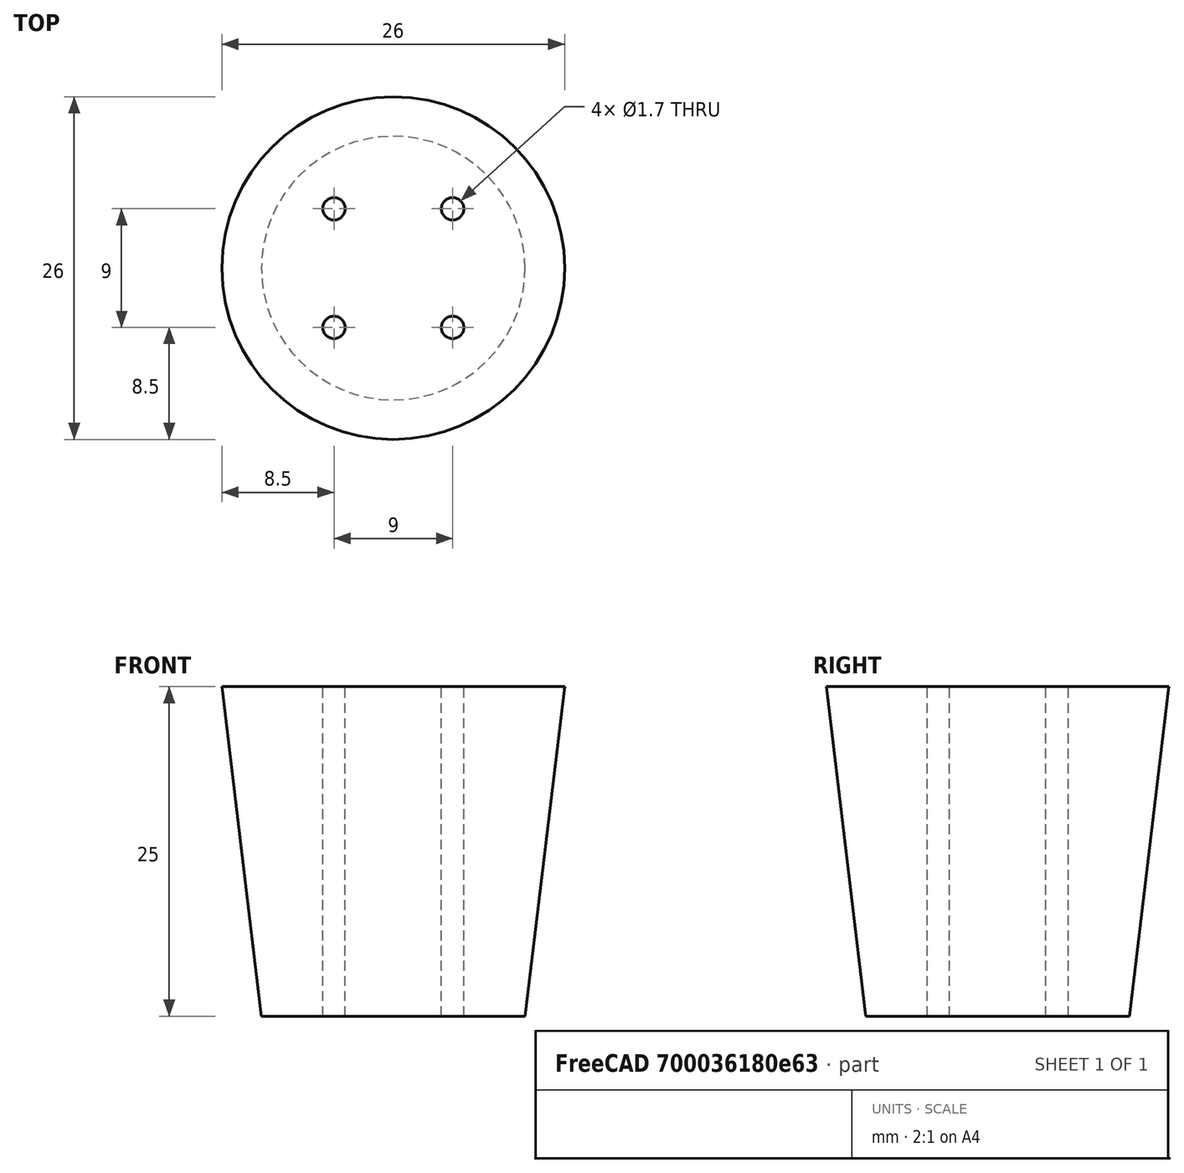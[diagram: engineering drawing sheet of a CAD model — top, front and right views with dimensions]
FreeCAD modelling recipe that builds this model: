
FCSTD DOCUMENT  (FreeCAD 0.18R15938 (Git))
Label: plug
License: All rights reserved
LicenseURL: http://en.wikipedia.org/wiki/All_rights_reserved
objects: Drawing::FeatureViewPython×13, TechDraw::DrawViewDimension×9, TechDraw::DrawProjGroupItem×6, TechDraw::DrawSVGTemplate×3, Drawing::FeatureViewPart×3, TechDraw::DrawPage×3, TechDraw::DrawProjGroup×2, PartDesign::AdditiveCone×1, PartDesign::SubtractiveCylinder×1, PartDesign::PolarPattern×1, PartDesign::Body×1, Drawing::FeaturePage×1, TechDraw::DrawGeomHatch×1, TechDraw::DrawViewSection×1, TechDraw::DrawViewAnnotation×1
note: 6 computed .brp shape members not serialized (recipe doc carries the construction recipe); baked Part::Feature solids carry a one-line shape summary decoded from their .brp

FEATURE [PartDesign::AdditiveCone] Cone
  Angle = 360
  AttacherType = Attacher::AttachEngine3D
  Height = 25
  Radius1 = 10
  Radius2 = 13
FEATURE [PartDesign::SubtractiveCylinder] Cylinder001  label="hole"
  Angle = 360
  AttacherType = Attacher::AttachEngine3D
  AttachmentOffset = pos=(4.5,4.5,0) rot=(0,0,1;0rad)
  BaseFeature = -> Cone
  Height = 50
  MapMode = 5
  Placement = pos=(4.5,4.5,0) rot=(0,0,1;0rad)
  Radius = 0.85
  Support = -> [XY_Plane]
FEATURE [PartDesign::PolarPattern] PolarPattern
  Angle = 360
  Axis = -> Z_Axis
  BaseFeature = -> Cylinder001
  Occurrences = 4
  Originals = -> [Cylinder001]
  Placement = pos=(4.5,4.5,0) rot=(0,0,1;0rad)
FEATURE [PartDesign::Body] Body
  Group = -> [Cone,Cylinder001,PolarPattern]
  Origin = -> Origin
  Tip = -> PolarPattern
FEATURE [TechDraw::DrawSVGTemplate] Template
  EditableTexts = Designed_by_Name=Christian <owner>; Drawing_number=2; FC-Date=21.2.2019; FC-SC=2:1; FC-SH=1; FC-Title=Title; Subtitle=silicone plug; Weight=Weight
  Height = 210
  Orientation = 1
  Width = 297
FEATURE [TechDraw::DrawProjGroupItem] ProjItem
  CoarseView = false
  Direction = (0,-1,0)
  Focus = 100
  HardHidden = true
  IsoCount = 0
  IsoHidden = true
  IsoVisible = false
  LockPosition = true
  Perspective = false
  Rotation = 0
  RotationVector = (1,0,0)
  Scale = 2
  ScaleType = 2
  SeamHidden = false
  SeamVisible = true
  SmoothHidden = true
  SmoothVisible = false
  Source = -> [PolarPattern]
  Type = 0
  X = 0
  Y = 0
FEATURE [TechDraw::DrawProjGroupItem] ProjItem003
  CoarseView = false
  Direction = (1,-1,-1)
  Focus = 100
  HardHidden = false
  IsoCount = 0
  IsoHidden = false
  IsoVisible = false
  LockPosition = true
  Perspective = false
  Rotation = 0
  RotationVector = (1,1,0)
  Scale = 2
  ScaleType = 2
  SeamHidden = false
  SeamVisible = false
  SmoothHidden = false
  SmoothVisible = false
  Source = -> [PolarPattern]
  Type = 9
  X = 124.084
  Y = -2.07724
FEATURE [TechDraw::DrawProjGroupItem] ProjItem004
  CoarseView = false
  Direction = (0,0,1)
  Focus = 100
  HardHidden = false
  IsoCount = 1
  IsoHidden = false
  IsoVisible = false
  LockPosition = false
  Perspective = false
  Rotation = 0
  RotationVector = (1,0,0)
  Scale = 2
  ScaleType = 2
  SeamHidden = false
  SeamVisible = false
  SmoothHidden = false
  SmoothVisible = false
  Source = -> [PolarPattern]
  Type = 4
  X = 0
  Y = -82.3829
FEATURE [TechDraw::DrawProjGroup] ProjGroup
  Anchor = -> ProjItem
  AutoDistribute = true
  LockPosition = false
  ProjectionType = 0
  Rotation = 0
  Scale = 2
  ScaleType = 2
  Source = -> [PolarPattern]
  Views = -> [ProjItem,ProjItem003,ProjItem004]
  X = 78.42
  Y = 143.503
  spacingX = 15
  spacingY = 15
FEATURE [TechDraw::DrawViewDimension] Dimension001
  Arbitrary = false
  FormatSpec = %.2f
  LockPosition = false
  MeasureType = 1
  OverTolerance = 0
  References2D = -> [ProjItem]
  Rotation = 0
  ScaleType = 0
  Type = 1
  UnderTolerance = 0
  X = 0.238546
  Y = -38.9683
FEATURE [TechDraw::DrawViewDimension] Dimension002
  Arbitrary = false
  FormatSpec = %.2f
  LockPosition = false
  MeasureType = 1
  OverTolerance = 0
  References2D = -> [ProjItem]
  Rotation = 0
  ScaleType = 0
  Type = 1
  UnderTolerance = 0
  X = 1.55225
  Y = 47.0944
FEATURE [TechDraw::DrawViewDimension] Dimension004
  Arbitrary = false
  FormatSpec = %.2f
  LockPosition = false
  MeasureType = 1
  OverTolerance = 0
  References2D = -> [ProjItem]
  Rotation = 0
  ScaleType = 0
  Type = 2
  UnderTolerance = 0
  X = -44.7315
  Y = -2.79405
FEATURE [TechDraw::DrawViewDimension] Dimension005
  Arbitrary = false
  FormatSpec = %.2f
  LockPosition = false
  MeasureType = 1
  OverTolerance = 0
  References2D = -> [ProjItem]
  Rotation = 0
  ScaleType = 0
  Type = 1
  UnderTolerance = 0
  X = -40.1485
  Y = 33.3646
FEATURE [TechDraw::DrawViewDimension] Dimension006
  Arbitrary = false
  FormatSpec = %.2f
  LockPosition = false
  MeasureType = 1
  OverTolerance = 0
  References2D = -> [ProjItem]
  Rotation = 0
  ScaleType = 0
  Type = 1
  UnderTolerance = 0
  X = 44.3913
  Y = 33.3822
FEATURE [Drawing::FeatureViewPart] Ortho  label="Ortho_0_0"
  Direction = (1,0,0)
  HiddenWidth = 0.15
  LineWidth = 0.35
  Rotation = -90
  Scale = 4
  ShowHiddenLines = true
  ShowSmoothLines = false
  Source = -> PolarPattern
  Tolerance = 0.05
  ViewResult = <blob: 8468 chars omitted>
  Visible = true
  X = 120
  Y = 264.67
FEATURE [Drawing::FeatureViewPart] Ortho002  label="Ortho_0_1"
  Direction = (0,0,1)
  HiddenWidth = 0.15
  LineWidth = 0.35
  Rotation = 90
  Scale = 4
  ShowHiddenLines = true
  ShowSmoothLines = false
  Source = -> PolarPattern
  Tolerance = 0.05
  ViewResult = <g id="Ortho_0_1"\n   transform="rotate(90,120,80.33) translate(120,80.33) scale(4,4)"\n  >\n<g   fill="none"\n   stroke="rgb(0, 0, 0)"\n   stroke-dasharray="0.2,0.1)"\n   stroke-linecap="butt"\n   stroke-linejoin="miter"\n   stroke-width="0.037500"\n   transform="scale(1,-1)"\n  >\n<circle cx ="0" cy ="0" r ="10" /><circle cx ="-4.5" cy ="-4.5" r ="0.85" /><circle cx ="4.5" cy ="-4.5" r ="0.85" /><circle cx ="4.5" cy ="4.5" r ="0.85" /><circle cx ="-4.5" cy ="4.5" r ="0.85" /></g>\n<g   fill="none"\n   stroke="rgb(0, 0, 0)"\n   stroke-linecap="butt"\n   stroke-linejoin="miter"\n   stroke-width="0.087500"\n   transform="scale(1,-1)"\n  >\n<circle cx ="0" cy ="0" r ="13" /><circle cx ="-4.5" cy ="-4.5" r ="0.85" /><circle cx ="4.5" cy ="-4.5" r ="0.85" /><circle cx ="-4.5" cy ="4.5" r ="0.85" /><circle cx ="4.5" cy ="4.5" r ="0.85" /></g>\n</g>
  Visible = true
  X = 120
  Y = 80.33
FEATURE [Drawing::FeatureViewPart] Ortho003  label="Ortho_1_1"
  Direction = (0.57735,0.57735,0.57735)
  HiddenWidth = 0.15
  LineWidth = 0.35
  Rotation = 120
  Scale = 4
  ShowHiddenLines = true
  ShowSmoothLines = false
  Source = -> PolarPattern
  Tolerance = 0.05
  ViewResult = <blob: 3528 chars omitted>
  Visible = true
  X = 294
  Y = 139.16
FEATURE [Drawing::FeatureViewPython] dim002  # drawing view (typed FeaturePython)
  Rotation = 0
  ViewResult = <g> \n  <line x1="118.000000" y1="132.330000" x2="37.053954" y2="132.330000" style="stroke:rgb(0,0,255);stroke-width:0.50" />\n<line x1="118.000000" y1="28.330000" x2="37.053954" y2="28.330000" style="stroke:rgb(0,0,255);stroke-width:0.50" />\n<line x1="38.053954" y1="132.330000" x2="38.053954" y2="28.330000" style="stroke:rgb(0,0,255);stroke-width:0.50" /> \n  <polygon points="38.053954,28.330000 37.053954,31.330000 38.053954,32.330000 39.053954,31.330000" style="fill:rgb(0,0,255);stroke:rgb(0,0,255);stroke-width:0" /><polygon points="38.053954,132.330000 39.053954,129.330000 38.053954,128.330000 37.053954,129.330000" style="fill:rgb(0,0,255);stroke:rgb(0,0,255);stroke-width:0" /> \n  <text x="36.053954" y="80.330000" font-family="inherit" font-size="3.6" fill="rgb(0,0,255)" text-anchor="middle" transform="rotate(-90.000000 36.053954,80.330000)" >26</text> </g>
  Visible = true
  X = 0
  Y = 0
  arrowL1 = 3
  arrowL2 = 1
  arrowW = 2
  arrow_scheme = 0
  autoPlaceOffset = 2
  autoPlaceText = true
  click1_x = 38.054
  click1_y = 40.1287
  click2_x = 38.054
  click2_y = 40.1287
  comma_decimal_place = false
  dimension_line_overshoot = 1
  gap_datum_points = 2
  halfDimension_linear = false
  lineColor = rgb(0,0,255)
  strokeWidth = 0.5
  textFormat_linear = %(value)3.3f
  textRenderer_color = rgb(0,0,255)
  textRenderer_family = inherit
  textRenderer_size = 3.6
  unit_custom_scale = 1
  unit_scheme = 0
FEATURE [Drawing::FeatureViewPython] dim004  # drawing view (typed FeaturePython)
  Rotation = 0
  ViewResult = <g> \n  <line x1="66.326800" y1="164.670000" x2="51.366021" y2="164.670000" style="stroke:rgb(0,0,255);stroke-width:0.50" />\n<line x1="78.251520" y1="264.670000" x2="51.366021" y2="264.670000" style="stroke:rgb(0,0,255);stroke-width:0.50" />\n<line x1="52.366021" y1="164.670000" x2="52.366021" y2="264.670000" style="stroke:rgb(0,0,255);stroke-width:0.50" /> \n  <polygon points="52.366021,264.670000 53.366021,261.670000 52.366021,260.670000 51.366021,261.670000" style="fill:rgb(0,0,255);stroke:rgb(0,0,255);stroke-width:0" /><polygon points="52.366021,164.670000 51.366021,167.670000 52.366021,168.670000 53.366021,167.670000" style="fill:rgb(0,0,255);stroke:rgb(0,0,255);stroke-width:0" /> \n  <text x="50.366021" y="214.670000" font-family="inherit" font-size="3.6" fill="rgb(0,0,255)" text-anchor="middle" transform="rotate(-90.000000 50.366021,214.670000)" >25</text> </g>
  Visible = true
  X = 0
  Y = 0
  arrowL1 = 3
  arrowL2 = 1
  arrowW = 2
  arrow_scheme = 0
  autoPlaceOffset = 2
  autoPlaceText = true
  click1_x = 52.366
  click1_y = 213.983
  click2_x = 52.366
  click2_y = 213.983
  comma_decimal_place = false
  dimension_line_overshoot = 1
  gap_datum_points = 2
  halfDimension_linear = false
  lineColor = rgb(0,0,255)
  strokeWidth = 0.5
  textFormat_linear = %(value)3.3f
  textRenderer_color = rgb(0,0,255)
  textRenderer_family = inherit
  textRenderer_size = 3.6
  unit_custom_scale = 1
  unit_scheme = 0
FEATURE [TechDraw::DrawSVGTemplate] Template001
  EditableTexts = Designed_by_Name=Designed by Name; Drawing_number=Drawing number; FC-Date=Date; FC-SC=Scale; FC-SH=Sheet; FC-Title=Title; Subtitle=Subtitle; Weight=Weight
  Height = 210
  Orientation = 1
  Width = 297
FEATURE [TechDraw::DrawProjGroupItem] ProjItem005  label="Front"
  CoarseView = false
  Direction = (0,-1,0)
  Focus = 100
  HardHidden = false
  IsoCount = 0
  IsoHidden = false
  IsoVisible = false
  LockPosition = true
  Perspective = false
  Rotation = 0
  RotationVector = (1,0,0)
  Scale = 2
  ScaleType = 2
  SeamHidden = false
  SeamVisible = false
  SmoothHidden = false
  SmoothVisible = false
  Source = -> [PolarPattern]
  Type = 0
  X = 0
  Y = 0
FEATURE [TechDraw::DrawProjGroupItem] ProjItem007  label="Bottom"
  CoarseView = false
  Direction = (0,0,-1)
  Focus = 100
  HardHidden = false
  IsoCount = 0
  IsoHidden = false
  IsoVisible = false
  LockPosition = false
  Perspective = false
  Rotation = 0
  RotationVector = (1,0,0)
  Scale = 2
  ScaleType = 2
  SeamHidden = false
  SeamVisible = false
  SmoothHidden = false
  SmoothVisible = false
  Source = -> [PolarPattern]
  Type = 5
  X = 0
  Y = 82.3829
FEATURE [TechDraw::DrawProjGroupItem] ProjItem008  label="FrontBottomLeft"
  CoarseView = false
  Direction = (-1,-1,-1)
  Focus = 100
  HardHidden = false
  IsoCount = 0
  IsoHidden = false
  IsoVisible = false
  LockPosition = false
  Perspective = false
  Rotation = 0
  RotationVector = (1,-1,0)
  Scale = 2
  ScaleType = 2
  SeamHidden = false
  SeamVisible = false
  SmoothHidden = false
  SmoothVisible = false
  Source = -> [PolarPattern]
  Type = 8
  X = 82.3829
  Y = 82.3829
FEATURE [TechDraw::DrawProjGroup] ProjGroup001
  Anchor = -> ProjItem005
  AutoDistribute = true
  LockPosition = false
  ProjectionType = 0
  Rotation = 0
  Scale = 2
  ScaleType = 0
  Source = -> [PolarPattern]
  Views = -> [ProjItem005,ProjItem007,ProjItem008]
  X = 62.8611
  Y = 69.42
  spacingX = 15
  spacingY = 15
FEATURE [TechDraw::DrawViewDimension] Dimension
  Arbitrary = false
  FormatSpec = %.2f
  LockPosition = false
  MeasureType = 1
  OverTolerance = 0
  References2D = -> [ProjItem005]
  Rotation = 0
  ScaleType = 0
  Type = 1
  UnderTolerance = 0
  X = 0.359317
  Y = -30.542
FEATURE [Drawing::FeatureViewPython] centerLines001  # drawing view (typed FeaturePython)
  Rotation = 0
  ViewResult = <g transform="scale(4.000000,4.000000)" stroke="rgb(0,0,255)"  stroke-width="0.080000" > <path d="M 35.350000,24.582500 L 35.350000,25.332500 M 35.350000,25.832500 L 35.350000,27.332500 M 35.350000,27.832500 L 35.350000,28.582500 M 35.350000,29.082500 L 35.350000,30.582500 M 35.350000,31.082500 L 35.350000,31.832500 M 35.350000,32.332500 L 35.350000,33.832500 M 35.350000,34.332500 L 35.350000,35.082500 M 35.350000,35.582500 L 35.350000,36.548504 "/>\n<path d="M 35.350000,24.582500 L 35.350000,25.332500 M 35.350000,25.832500 L 35.350000,27.332500 M 35.350000,27.832500 L 35.350000,28.582500 M 35.350000,29.082500 L 35.350000,30.582500 M 35.350000,31.082500 L 35.350000,31.832500 M 35.350000,32.332500 L 35.350000,33.832500 M 35.350000,34.332500 L 35.350000,35.082500 "/> </g> 
  Visible = true
  X = 0
  Y = 0
  centerLine_color = rgb(0,0,255)
  centerLine_len_dash = 6
  centerLine_len_dot = 3
  centerLine_len_gap = 2
  centerLine_width = 0.32
  click1_x = 136.029
  click1_y = 146.194
  click2_x = 153.742
  click2_y = 140.618
FEATURE [Drawing::FeatureViewPython] centerLines002  # drawing view (typed FeaturePython)
  Rotation = 0
  ViewResult = <g transform="scale(4.000000,4.000000)" stroke="rgb(0,0,255)"  stroke-width="0.080000" > <path d="M 33.650000,24.582500 L 33.650000,25.332500 M 33.650000,25.832500 L 33.650000,27.332500 M 33.650000,27.832500 L 33.650000,28.582500 M 33.650000,29.082500 L 33.650000,30.582500 M 33.650000,31.082500 L 33.650000,31.832500 M 33.650000,32.332500 L 33.650000,33.832500 M 33.650000,34.332500 L 33.650000,35.082500 M 33.650000,35.582500 L 33.650000,36.630507 "/>\n<path d="M 33.650000,24.582500 L 33.650000,25.332500 M 33.650000,25.832500 L 33.650000,27.332500 M 33.650000,27.832500 L 33.650000,28.266215 "/> </g> 
  Visible = true
  X = 0
  Y = 0
  centerLine_color = rgb(0,0,255)
  centerLine_len_dash = 6
  centerLine_len_dot = 3
  centerLine_len_gap = 2
  centerLine_width = 0.32
  click1_x = 139.309
  click1_y = 146.522
  click2_x = 165.55
  click2_y = 113.065
FEATURE [Drawing::FeatureViewPython] centerLines003  # drawing view (typed FeaturePython)
  Rotation = 0
  ViewResult = <g transform="scale(4.000000,4.000000)" stroke="rgb(0,0,255)"  stroke-width="0.080000" > <path d="M 26.350000,24.582500 L 26.350000,25.332500 M 26.350000,25.832500 L 26.350000,27.332500 M 26.350000,27.832500 L 26.350000,28.582500 M 26.350000,29.082500 L 26.350000,30.582500 M 26.350000,31.082500 L 26.350000,31.832500 M 26.350000,32.332500 L 26.350000,33.832500 M 26.350000,34.332500 L 26.350000,35.082500 M 26.350000,35.582500 L 26.350000,36.630507 "/>\n<path d="M 26.350000,24.582500 L 26.350000,25.332500 M 26.350000,25.832500 L 26.350000,27.332500 M 26.350000,27.832500 L 26.350000,28.582500 M 26.350000,29.082500 L 26.350000,30.582500 M 26.350000,31.082500 L 26.350000,31.832500 M 26.350000,32.332500 L 26.350000,33.832500 M 26.350000,34.332500 L 26.350000,35.082500 M 26.350000,35.582500 L 26.350000,36.712510 "/> </g> 
  Visible = true
  X = 0
  Y = 0
  centerLine_color = rgb(0,0,255)
  centerLine_len_dash = 6
  centerLine_len_dot = 3
  centerLine_len_gap = 2
  centerLine_width = 0.32
  click1_x = 109.132
  click1_y = 146.522
  click2_x = 108.804
  click2_y = 146.85
FEATURE [Drawing::FeatureViewPython] centerLines004  # drawing view (typed FeaturePython)
  Rotation = 0
  ViewResult = <g transform="scale(4.000000,4.000000)" stroke="rgb(0,0,255)"  stroke-width="0.080000" > <path d="M 24.650000,24.582500 L 24.650000,25.332500 M 24.650000,25.832500 L 24.650000,27.332500 M 24.650000,27.832500 L 24.650000,28.582500 M 24.650000,29.082500 L 24.650000,30.582500 M 24.650000,31.082500 L 24.650000,31.832500 M 24.650000,32.332500 L 24.650000,33.832500 M 24.650000,34.332500 L 24.650000,35.082500 M 24.650000,35.582500 L 24.650000,36.548504 "/>\n<path d="M 24.650000,24.582500 L 24.650000,25.332500 M 24.650000,25.832500 L 24.650000,27.332500 M 24.650000,27.832500 L 24.650000,28.582500 M 24.650000,29.082500 L 24.650000,30.582500 M 24.650000,31.082500 L 24.650000,31.832500 M 24.650000,32.332500 L 24.650000,33.104384 "/> </g> 
  Visible = true
  X = 0
  Y = 0
  centerLine_color = rgb(0,0,255)
  centerLine_len_dash = 6
  centerLine_len_dot = 3
  centerLine_len_gap = 2
  centerLine_width = 0.32
  click1_x = 99.9477
  click1_y = 146.194
  click2_x = 92.4034
  click2_y = 132.418
FEATURE [Drawing::FeatureViewPython] dim005  # drawing view (typed FeaturePython)
  Rotation = 0
  ViewResult = <g> \n  <line x1="160.000000" y1="266.670000" x2="160.000000" y2="283.759200" style="stroke:rgb(0,0,255);stroke-width:0.50" />\n<line x1="80.000000" y1="266.670000" x2="80.000000" y2="283.759200" style="stroke:rgb(0,0,255);stroke-width:0.50" />\n<line x1="160.000000" y1="282.759200" x2="80.000000" y2="282.759200" style="stroke:rgb(0,0,255);stroke-width:0.50" /> \n  <polygon points="80.000000,282.759200 83.000000,283.759200 84.000000,282.759200 83.000000,281.759200" style="fill:rgb(0,0,255);stroke:rgb(0,0,255);stroke-width:0" /><polygon points="160.000000,282.759200 157.000000,281.759200 156.000000,282.759200 157.000000,283.759200" style="fill:rgb(0,0,255);stroke:rgb(0,0,255);stroke-width:0" /> \n  <text x="120.000000" y="280.759200" font-family="inherit" font-size="3.6" fill="rgb(0,0,255)" text-anchor="middle" transform="rotate(-0.000000 120.000000,280.759200)" >20</text> </g>
  Visible = true
  X = 0
  Y = 0
  arrowL1 = 3
  arrowL2 = 1
  arrowW = 2
  arrow_scheme = 0
  autoPlaceOffset = 2
  autoPlaceText = true
  click1_x = 75.5331
  click1_y = 282.759
  click2_x = 75.5331
  click2_y = 282.759
  comma_decimal_place = false
  dimension_line_overshoot = 1
  gap_datum_points = 2
  halfDimension_linear = false
  lineColor = rgb(0,0,255)
  strokeWidth = 0.5
  textFormat_linear = %(value)3.3f
  textRenderer_color = rgb(0,0,255)
  textRenderer_family = inherit
  textRenderer_size = 3.6
  unit_custom_scale = 1.3
  unit_scheme = 0
FEATURE [Drawing::FeatureViewPython] dim001  # drawing view (typed FeaturePython)
  Rotation = 0
  ViewResult = <g> \n  <line x1="68.000000" y1="162.670000" x2="68.000000" y2="156.696284" style="stroke:rgb(0,0,255);stroke-width:0.50" />\n<line x1="172.000000" y1="162.670000" x2="172.000000" y2="156.696284" style="stroke:rgb(0,0,255);stroke-width:0.50" />\n<line x1="68.000000" y1="157.696284" x2="172.000000" y2="157.696284" style="stroke:rgb(0,0,255);stroke-width:0.50" /> \n  <polygon points="172.000000,157.696284 169.000000,156.696284 168.000000,157.696284 169.000000,158.696284" style="fill:rgb(0,0,255);stroke:rgb(0,0,255);stroke-width:0" /><polygon points="68.000000,157.696284 71.000000,158.696284 72.000000,157.696284 71.000000,156.696284" style="fill:rgb(0,0,255);stroke:rgb(0,0,255);stroke-width:0" /> \n  <text x="120.000000" y="155.696284" font-family="inherit" font-size="3.6" fill="rgb(0,0,255)" text-anchor="middle" transform="rotate(0.000000 120.000000,155.696284)" >26</text> </g>
  Visible = true
  X = 0
  Y = 0
  arrowL1 = 3
  arrowL2 = 1
  arrowW = 2
  arrow_scheme = 0
  autoPlaceOffset = 2
  autoPlaceText = true
  click1_x = 163.18
  click1_y = 157.696
  click2_x = 163.18
  click2_y = 157.696
  comma_decimal_place = false
  dimension_line_overshoot = 1
  gap_datum_points = 2
  halfDimension_linear = false
  lineColor = rgb(0,0,255)
  strokeWidth = 0.5
  textFormat_linear = %(value)3.3f
  textRenderer_color = rgb(0,0,255)
  textRenderer_family = inherit
  textRenderer_size = 3.6
  unit_custom_scale = 1
  unit_scheme = 0
FEATURE [Drawing::FeatureViewPython] dia001  # drawing view (typed FeaturePython)
  Rotation = 0
  ViewResult = <g>  <circle cx ="138.000000" cy ="98.330000" r="0.250000" stroke="none" fill="rgb(0,0,255)" /> \n<line x1="164.648471" y1="38.150256" x2="136.623362" y2="101.438837" style="stroke:rgb(0,0,255);stroke-width:0.50" />\n<polygon points="139.376638,95.221163 141.505683,92.882965 140.996213,91.563708 139.676956,92.073178" style="fill:rgb(0,0,255);stroke:rgb(0,0,255);stroke-width:0" />\n<polygon points="136.623362,101.438837 134.494317,103.777035 135.003787,105.096292 136.323044,104.586822" style="fill:rgb(0,0,255);stroke:rgb(0,0,255);stroke-width:0" />\n<line x1="164.648471" y1="38.150256" x2="201.192400" y2="38.150256" style="stroke:rgb(0,0,255);stroke-width:0.50" />\n<text x="182.920436" y="36.150256" font-family="inherit" font-size="3.6" fill="rgb(0,0,255)" text-anchor="middle" transform="rotate(0.000000 182.920436,36.150256)" >Ø1.7</text> </g>
  Visible = false
  X = 0
  Y = 0
  arrowL1 = 3
  arrowL2 = 1
  arrowW = 2
  arrow_scheme = 0
  autoPlaceOffset = 2
  autoPlaceText = true
  centerPointDia = 0.5
  click1_x = 164.648
  click1_y = 38.1503
  click2_x = 201.192
  click2_y = 39.7566
  click3_x = 201.192
  click3_y = 39.7566
  comma_decimal_place = false
  lineColor = rgb(0,0,255)
  strokeWidth = 0.5
  textFormat_circular = Ø%(value)3.3f
  textRenderer_color = rgb(0,0,255)
  textRenderer_family = inherit
  textRenderer_size = 3.6
  unit_custom_scale = 1
  unit_scheme = 0
FEATURE [Drawing::FeatureViewPython] dim003  # drawing view (typed FeaturePython)
  Rotation = 0
  ViewResult = <g> \n  <line x1="134.600000" y1="144.522028" x2="134.600000" y2="137.744965" style="stroke:rgb(0,0,255);stroke-width:0.50" />\n<line x1="141.400000" y1="144.194016" x2="141.400000" y2="137.744965" style="stroke:rgb(0,0,255);stroke-width:0.50" />\n<line x1="134.600000" y1="138.744965" x2="141.400000" y2="138.744965" style="stroke:rgb(0,0,255);stroke-width:0.50" /> \n  <polygon points="141.400000,138.744965 144.400000,139.744965 145.400000,138.744965 144.400000,137.744965" style="fill:rgb(0,0,255);stroke:rgb(0,0,255);stroke-width:0" /><polygon points="134.600000,138.744965 131.600000,137.744965 130.600000,138.744965 131.600000,139.744965" style="fill:rgb(0,0,255);stroke:rgb(0,0,255);stroke-width:0" /> \n  <text x="138.000000" y="136.744965" font-family="inherit" font-size="3.6" fill="rgb(0,0,255)" text-anchor="middle" transform="rotate(0.000000 138.000000,136.744965)" >1.7</text> </g>
  Visible = true
  X = 0
  Y = 0
  arrowL1 = 3
  arrowL2 = 1
  arrowW = 2
  arrow_scheme = 0
  autoPlaceOffset = 2
  autoPlaceText = true
  click1_x = 134.6
  click1_y = 138.745
  click2_x = 134.6
  click2_y = 138.745
  comma_decimal_place = false
  dimension_line_overshoot = 1
  gap_datum_points = 2
  halfDimension_linear = false
  lineColor = rgb(0,0,255)
  strokeWidth = 0.5
  textFormat_linear = %(value)3.3f
  textRenderer_color = rgb(0,0,255)
  textRenderer_family = inherit
  textRenderer_size = 3.6
  unit_custom_scale = 1
  unit_scheme = 0
FEATURE [Drawing::FeatureViewPython] dim006  # drawing view (typed FeaturePython)
  Rotation = 0
  ViewResult = <g> \n  <line x1="98.600000" y1="144.194016" x2="98.600000" y2="138.793567" style="stroke:rgb(0,0,255);stroke-width:0.50" />\n<line x1="105.400000" y1="144.522028" x2="105.400000" y2="138.793567" style="stroke:rgb(0,0,255);stroke-width:0.50" />\n<line x1="98.600000" y1="139.793567" x2="105.400000" y2="139.793567" style="stroke:rgb(0,0,255);stroke-width:0.50" /> \n  <polygon points="105.400000,139.793567 108.400000,140.793567 109.400000,139.793567 108.400000,138.793567" style="fill:rgb(0,0,255);stroke:rgb(0,0,255);stroke-width:0" /><polygon points="98.600000,139.793567 95.600000,138.793567 94.600000,139.793567 95.600000,140.793567" style="fill:rgb(0,0,255);stroke:rgb(0,0,255);stroke-width:0" /> \n  <text x="102.000000" y="137.793567" font-family="inherit" font-size="3.6" fill="rgb(0,0,255)" text-anchor="middle" transform="rotate(0.000000 102.000000,137.793567)" >1.7</text> </g>
  Visible = true
  X = 0
  Y = 0
  arrowL1 = 3
  arrowL2 = 1
  arrowW = 2
  arrow_scheme = 0
  autoPlaceOffset = 2
  autoPlaceText = true
  click1_x = 98.6
  click1_y = 139.794
  click2_x = 98.6
  click2_y = 139.794
  comma_decimal_place = false
  dimension_line_overshoot = 1
  gap_datum_points = 2
  halfDimension_linear = false
  lineColor = rgb(0,0,255)
  strokeWidth = 0.5
  textFormat_linear = %(value)3.3f
  textRenderer_color = rgb(0,0,255)
  textRenderer_family = inherit
  textRenderer_size = 3.6
  unit_custom_scale = 1
  unit_scheme = 0
FEATURE [Drawing::FeatureViewPython] dim007  # drawing view (typed FeaturePython)
  Rotation = 0
  ViewResult = <g> \n  <line x1="105.400000" y1="100.330000" x2="105.400000" y2="146.691755" style="stroke:rgb(0,0,255);stroke-width:0.50" />\n<line x1="134.600000" y1="100.330000" x2="134.600000" y2="146.691755" style="stroke:rgb(0,0,255);stroke-width:0.50" />\n<line x1="105.400000" y1="145.691755" x2="134.600000" y2="145.691755" style="stroke:rgb(0,0,255);stroke-width:0.50" /> \n  <polygon points="134.600000,145.691755 131.600000,144.691755 130.600000,145.691755 131.600000,146.691755" style="fill:rgb(0,0,255);stroke:rgb(0,0,255);stroke-width:0" /><polygon points="105.400000,145.691755 108.400000,146.691755 109.400000,145.691755 108.400000,144.691755" style="fill:rgb(0,0,255);stroke:rgb(0,0,255);stroke-width:0" /> \n  <text x="120.000000" y="143.691755" font-family="inherit" font-size="3.6" fill="rgb(0,0,255)" text-anchor="middle" transform="rotate(0.000000 120.000000,143.691755)" >7.3</text> </g>
  Visible = true
  X = 0
  Y = 0
  arrowL1 = 3
  arrowL2 = 1
  arrowW = 2
  arrow_scheme = 0
  autoPlaceOffset = 2
  autoPlaceText = true
  click1_x = 137.491
  click1_y = 145.692
  click2_x = 137.491
  click2_y = 145.692
  comma_decimal_place = false
  dimension_line_overshoot = 1
  gap_datum_points = 2
  halfDimension_linear = false
  lineColor = rgb(0,0,255)
  strokeWidth = 0.5
  textFormat_linear = %(value)3.3f
  textRenderer_color = rgb(0,0,255)
  textRenderer_family = inherit
  textRenderer_size = 3.6
  unit_custom_scale = 1
  unit_scheme = 0
FEATURE [Drawing::FeatureViewPython] dim008  # drawing view (typed FeaturePython)
  Rotation = 0
  ViewResult = <g> \n  <line x1="141.400000" y1="100.330000" x2="141.400000" y2="146.145069" style="stroke:rgb(0,0,255);stroke-width:0.50" />\n<line x1="172.000000" y1="82.330000" x2="172.000000" y2="146.145069" style="stroke:rgb(0,0,255);stroke-width:0.50" />\n<line x1="141.400000" y1="145.145069" x2="172.000000" y2="145.145069" style="stroke:rgb(0,0,255);stroke-width:0.50" /> \n  <polygon points="172.000000,145.145069 169.000000,144.145069 168.000000,145.145069 169.000000,146.145069" style="fill:rgb(0,0,255);stroke:rgb(0,0,255);stroke-width:0" /><polygon points="141.400000,145.145069 144.400000,146.145069 145.400000,145.145069 144.400000,144.145069" style="fill:rgb(0,0,255);stroke:rgb(0,0,255);stroke-width:0" /> \n  <text x="156.700000" y="143.145069" font-family="inherit" font-size="3.6" fill="rgb(0,0,255)" text-anchor="middle" transform="rotate(0.000000 156.700000,143.145069)" >7.65</text> </g>
  Visible = true
  X = 0
  Y = 0
  arrowL1 = 3
  arrowL2 = 1
  arrowW = 2
  arrow_scheme = 0
  autoPlaceOffset = 2
  autoPlaceText = true
  click1_x = 161.272
  click1_y = 145.145
  click2_x = 161.272
  click2_y = 145.145
  comma_decimal_place = false
  dimension_line_overshoot = 1
  gap_datum_points = 2
  halfDimension_linear = false
  lineColor = rgb(0,0,255)
  strokeWidth = 0.5
  textFormat_linear = %(value)3.3f
  textRenderer_color = rgb(0,0,255)
  textRenderer_family = inherit
  textRenderer_size = 3.6
  unit_custom_scale = 1
  unit_scheme = 0
FEATURE [Drawing::FeaturePage] Page001
  EditableTexts = Christian <owner>  | 20.02.2019 | 4:1 | 2 | 1 | Silicone Plug
  Group = -> [Ortho,Ortho002,Ortho003,dim002,dim004,centerLines001,centerLines002,centerLines003,centerLines004,dim005,dim001,dia001,dim003,dim006,dim007,dim008]
  Template = <path>
FEATURE [TechDraw::DrawSVGTemplate] Template002
  EditableTexts = Designed_by_Name=Designed by Name; Drawing_number=Drawing number; FC-Date=Date; FC-SC=Scale; FC-SH=Sheet; FC-Title=Title; Subtitle=Subtitle; Weight=Weight
  Height = 210
  Orientation = 1
  Width = 297
FEATURE [TechDraw::DrawPage] Page003
  KeepUpdated = true
  ProjectionType = 0
  Template = -> Template002
FEATURE [TechDraw::DrawGeomHatch] GeomHatch  label="GeomHatchFX0"
  FilePattern = <path>
  NamePattern = Diamond
  ScalePattern = 1.4
  Source = -> ProjItem005 [Face0]
FEATURE [TechDraw::DrawViewSection] Section  label="Section A - A"
  BaseView = -> ProjItem007
  CoarseView = false
  Direction = (0,-1,0)
  FileHatchPattern = <path>
  Focus = 100
  HardHidden = false
  HatchScale = 9
  IsoCount = 0
  IsoHidden = false
  IsoVisible = false
  LockPosition = false
  NameGeomPattern = Diamond
  Perspective = false
  Rotation = 0
  ScaleType = 2
  SeamHidden = false
  SeamVisible = false
  SectionDirection = 3
  SectionNormal = (0,-1,0)
  SectionOrigin = (0,0,12.5)
  SectionSymbol = A
  SmoothHidden = false
  SmoothVisible = false
  Source = -> [PolarPattern]
  X = 158.559
  Y = 80.4124
FEATURE [TechDraw::DrawViewAnnotation] Annotation
  Font = osifont
  LineSpace = 80
  LockPosition = false
  MaxWidth = -1
  Rotation = 0
  ScaleType = 0
  Text = Default Text
  TextSize = 8
  TextStyle = 0
  X = 225.243
  Y = 156.411
FEATURE [TechDraw::DrawPage] Page002
  KeepUpdated = true
  ProjectionType = 0
  Template = -> Template001
  Views = -> [ProjGroup001,Dimension,Section,Annotation]
FEATURE [TechDraw::DrawViewDimension] Dimension007
  Arbitrary = false
  FormatSpec = %.2f
  LockPosition = false
  MeasureType = 1
  OverTolerance = 0
  References2D = -> [ProjItem]
  Rotation = 0
  ScaleType = 0
  Type = 1
  UnderTolerance = 0
  X = 38.9993
  Y = -31.4677
FEATURE [TechDraw::DrawViewDimension] Dimension009
  Arbitrary = false
  FormatSpec = %.2f
  LockPosition = false
  MeasureType = 1
  OverTolerance = 0
  References2D = -> [ProjItem004]
  Rotation = 0
  ScaleType = 0
  Type = 2
  UnderTolerance = 0
  X = -41.3933
  Y = 1.55225
FEATURE [TechDraw::DrawViewDimension] Dimension010
  Arbitrary = false
  FormatSpec = %.2f
  LockPosition = false
  MeasureType = 1
  OverTolerance = 0
  References2D = -> [ProjItem004]
  Rotation = 0
  ScaleType = 0
  Type = 2
  UnderTolerance = 0
  X = 36.7868
  Y = 0.747902
FEATURE [TechDraw::DrawPage] Page
  KeepUpdated = true
  ProjectionType = 0
  Template = -> Template
  Views = -> [ProjGroup,Dimension001,Dimension002,Dimension004,Dimension005,Dimension006,Dimension007,Dimension009,Dimension010]
note: 3 file-system paths scrubbed to <path> (originals preserved in the JSON sidecar)
